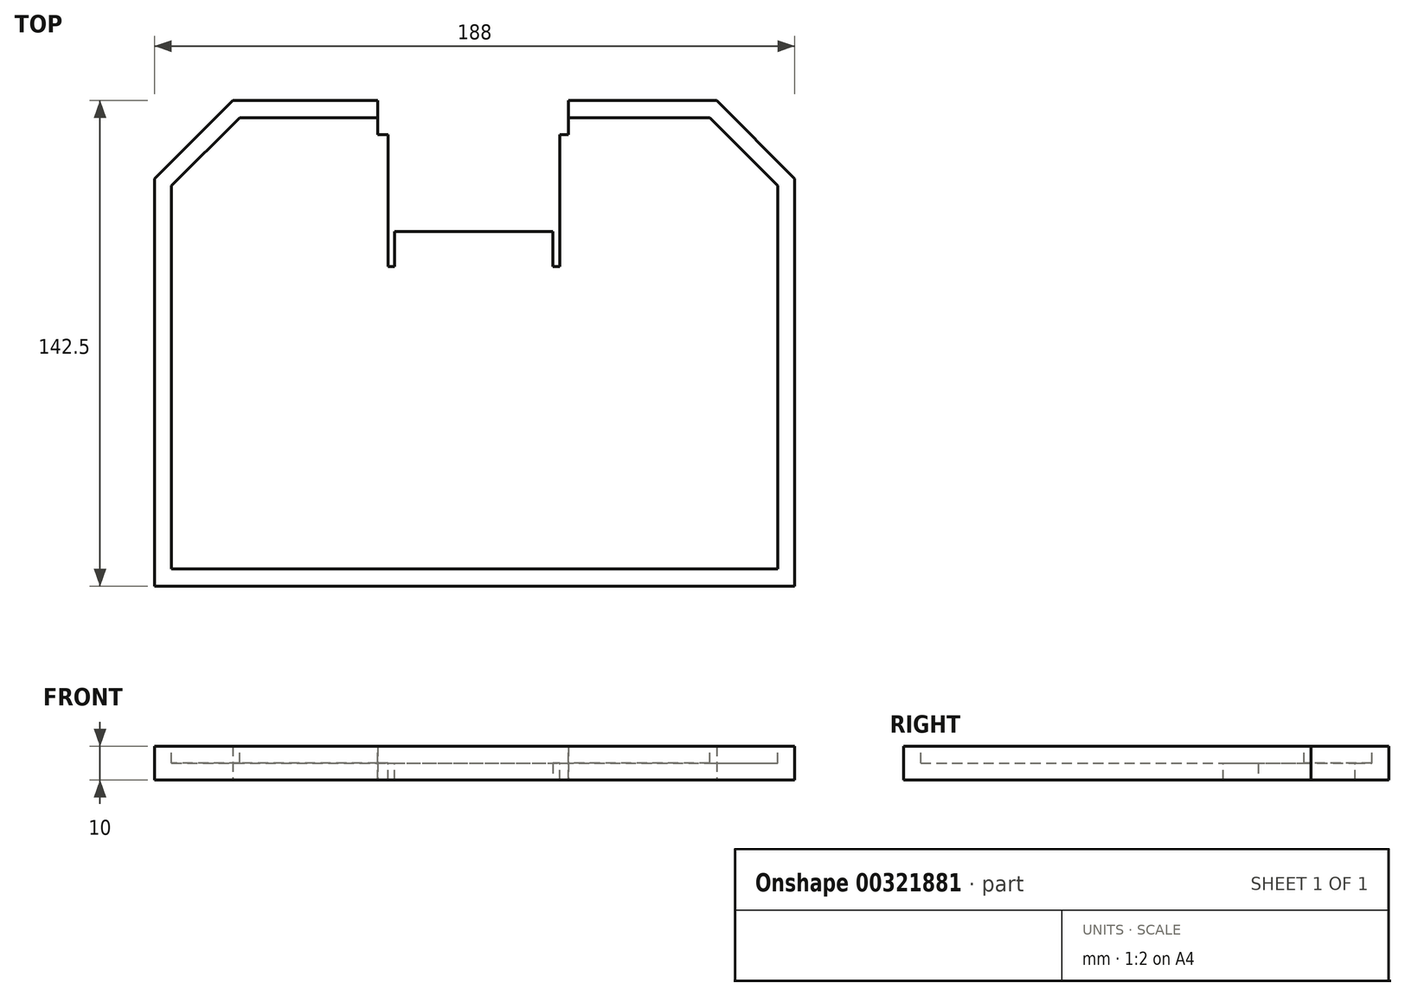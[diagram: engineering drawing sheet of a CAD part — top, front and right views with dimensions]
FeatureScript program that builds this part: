
annotation { "Feature Type Name" : "Feature", "Feature Type Description" : "" }
export const myFeature = defineFeature(function(context is Context, id is Id, definition is map)
    precondition{}
    {
        {
            var Q0;
            Q0=qCreatedBy(makeId("Top.planeOp"),FACE);
            var sketch = newSketch(context, id + "F0", { "sketchPlane" : qUnion([Q0])});
            skLineSegment(sketch, "E0.top", {"start": v(-156.06, -24.57) * mm, "end": v(31.94, -24.57) * mm});
            skLineSegment(sketch, "E1", {"start": v(-156.06, -24.57) * mm, "end": v(-156.06, 95) * mm});
            skLineSegment(sketch, "E2", {"start": v(-133.13, 117.93) * mm, "end": v(-156.06, 95) * mm});
            skLineSegment(sketch, "E3", {"start": v(31.94, 95) * mm, "end": v(31.94, -24.57) * mm});
            skLineSegment(sketch, "E4", {"start": v(9.01, 117.93) * mm, "end": v(31.94, 95) * mm});
            skLineSegment(sketch, "E5", {"start": v(9.01, 117.93) * mm, "end": v(-133.13, 117.93) * mm});
            skSolve(sketch);
        }
        {
            var Q0;
            Q0=makeQuery(id+"F0.imprint","IMPRINT",FACE,{"disambiguationData":[TD([[makeQuery(id+"F0.imprint","IMPRINT",EDGE,{"derivedFrom":sQuery(id+"F0.wireOp",EDGE,"E0.top")}),1.0]])]});
            extrude(context, id + "F1", {"entities" : qUnion([Q0]), "depth" : 10 * mm});
        }
        {
            var Q0;
            Q0=makeQuery(id+"F1.opExtrude","CAP_FACE",FACE,{"disambiguationData":[OSD([sQuery(id+"F0.wireOp",EDGE,"E0.top"),sQuery(id+"F0.wireOp",EDGE,"E1"),sQuery(id+"F0.wireOp",EDGE,"E2"),sQuery(id+"F0.wireOp",EDGE,"E3"),sQuery(id+"F0.wireOp",EDGE,"E4"),sQuery(id+"F0.wireOp",EDGE,"E5")])],"isStart":false});
            var sketch = newSketch(context, id + "F2", { "sketchPlane" : qUnion([Q0])});
            skLineSegment(sketch, "E6.0", {"start": v(6.94, 112.93) * mm, "end": v(26.94, 92.93) * mm});
            skLineSegment(sketch, "E6.1", {"start": v(-131.06, 112.93) * mm, "end": v(-151.06, 92.93) * mm});
            skLineSegment(sketch, "E6.2", {"start": v(-151.06, -19.57) * mm, "end": v(-151.06, 92.93) * mm});
            skLineSegment(sketch, "E6.3", {"start": v(6.94, 112.93) * mm, "end": v(-131.06, 112.93) * mm});
            skLineSegment(sketch, "E6.4", {"start": v(-151.06, -19.57) * mm, "end": v(26.94, -19.57) * mm});
            skLineSegment(sketch, "E6.5", {"start": v(26.94, 92.93) * mm, "end": v(26.94, -19.57) * mm});
            skSolve(sketch);
        }
        {
            var Q0;
            Q0 = qSketchRegion(id + "F2", true);
            extrude(context, id + "F3", {"entities" : qUnion([Q0]), "operationType" : NewBodyOperationType.REMOVE, "oppositeDirection" : true, "depth" : 5 * mm});
        }
        {
            var Q0;
            Q0=makeQuery(id+"F3.boolean.opBoolean","COPY",FACE,{"derivedFrom":makeQuery(id+"F3.opExtrude","CAP_FACE",FACE,{"disambiguationData":[OSD([sQuery(id+"F2.wireOp",EDGE,"E6.0"),sQuery(id+"F2.wireOp",EDGE,"E6.1"),sQuery(id+"F2.wireOp",EDGE,"E6.2"),sQuery(id+"F2.wireOp",EDGE,"E6.3"),sQuery(id+"F2.wireOp",EDGE,"E6.4"),sQuery(id+"F2.wireOp",EDGE,"E6.5")])],"isStart":false})});
            var sketch = newSketch(context, id + "F4", { "sketchPlane" : qUnion([Q0])});
            skLineSegment(sketch, "E7", {"start": v(-87.52, 69.23) * mm, "end": v(-85.52, 69.23) * mm});
            skLineSegment(sketch, "E8", {"start": v(26.94, 29.63) * mm, "end": v(-37.06, 29.63) * mm});
            skLineSegment(sketch, "E9", {"start": v(-37.06, 69.23) * mm, "end": v(-39.06, 69.23) * mm});
            skLineSegment(sketch, "E10", {"start": v(-87.52, 112.93) * mm, "end": v(-90.52, 112.93) * mm});
            skLineSegment(sketch, "E11", {"start": v(-90.52, 109.93) * mm, "end": v(-90.52, 107.93) * mm});
            skLineSegment(sketch, "E12", {"start": v(-34.52, 107.93) * mm, "end": v(-34.52, 109.93) * mm});
            skLineSegment(sketch, "E13", {"start": v(-34.52, 109.93) * mm, "end": v(-90.52, 109.93) * mm});
            skLineSegment(sketch, "E14", {"start": v(-34.52, 112.93) * mm, "end": v(6.94, 112.93) * mm});
            skLineSegment(sketch, "E15", {"start": v(-90.52, 112.93) * mm, "end": v(-131.06, 112.93) * mm});
            skLineSegment(sketch, "E16", {"start": v(-87.52, 109.93) * mm, "end": v(-90.52, 109.93) * mm});
            skLineSegment(sketch, "E17", {"start": v(-87.52, 107.93) * mm, "end": v(-90.52, 107.93) * mm});
            skLineSegment(sketch, "E18", {"start": v(-85.52, 107.93) * mm, "end": v(-39.06, 107.93) * mm});
            skLineSegment(sketch, "E19", {"start": v(-37.06, 107.93) * mm, "end": v(-34.52, 107.93) * mm});
            skLineSegment(sketch, "E20", {"start": v(-37.06, 69.23) * mm, "end": v(-37.06, 107.93) * mm});
            skLineSegment(sketch, "E21", {"start": v(-39.06, 69.23) * mm, "end": v(-39.06, 107.93) * mm});
            skLineSegment(sketch, "E22", {"start": v(-39.06, 69.23) * mm, "end": v(-37.06, 69.23) * mm});
            skLineSegment(sketch, "E23", {"start": v(-87.52, 69.23) * mm, "end": v(-87.52, 107.93) * mm});
            skLineSegment(sketch, "E24", {"start": v(-85.52, 69.23) * mm, "end": v(-85.52, 107.93) * mm});
            skSolve(sketch);
        }
        {
            var Q0;
            Q0 = qSketchRegion(id + "F4", true);
            extrude(context, id + "F5", {"entities" : qUnion([Q0]), "operationType" : NewBodyOperationType.REMOVE, "oppositeDirection" : true, "depth" : 5 * mm});
        }
        {
            var Q0;
            Q0=makeQuery(id+"F1.opExtrude","CAP_FACE",FACE,{"disambiguationData":[OSD([sQuery(id+"F0.wireOp",EDGE,"E0.top"),sQuery(id+"F0.wireOp",EDGE,"E1"),sQuery(id+"F0.wireOp",EDGE,"E2"),sQuery(id+"F0.wireOp",EDGE,"E3"),sQuery(id+"F0.wireOp",EDGE,"E4"),sQuery(id+"F0.wireOp",EDGE,"E5")])],"isStart":true});
            var sketch = newSketch(context, id + "F6", { "sketchPlane" : qUnion([Q0])});
            skLineSegment(sketch, "E25", {"start": v(-34.52, -109.93) * mm, "end": v(-34.52, -117.93) * mm});
            skLineSegment(sketch, "E26", {"start": v(-90.52, -109.93) * mm, "end": v(-90.52, -117.93) * mm});
            skLineSegment(sketch, "E27", {"start": v(-34.52, -117.93) * mm, "end": v(-90.52, -117.93) * mm});
            skLineSegment(sketch, "E28", {"start": v(-39.06, -79.49) * mm, "end": v(-85.52, -79.49) * mm});
            skLineSegment(sketch, "E29", {"start": v(-85.52, -79.49) * mm, "end": v(-85.52, -107.93) * mm});
            skLineSegment(sketch, "E30", {"start": v(-85.52, -107.93) * mm, "end": v(-39.06, -107.93) * mm});
            skLineSegment(sketch, "E31", {"start": v(-39.06, -107.93) * mm, "end": v(-39.06, -79.49) * mm});
            skLineSegment(sketch, "E32", {"start": v(-34.52, -109.93) * mm, "end": v(-90.52, -109.93) * mm});
            skSolve(sketch);
        }
        {
            var Q0;
            Q0 = qSketchRegion(id + "F6", true);
            extrude(context, id + "F7", {"entities" : qUnion([Q0]), "operationType" : NewBodyOperationType.REMOVE, "oppositeDirection" : true, "depth" : 10 * mm});
        }
    });
